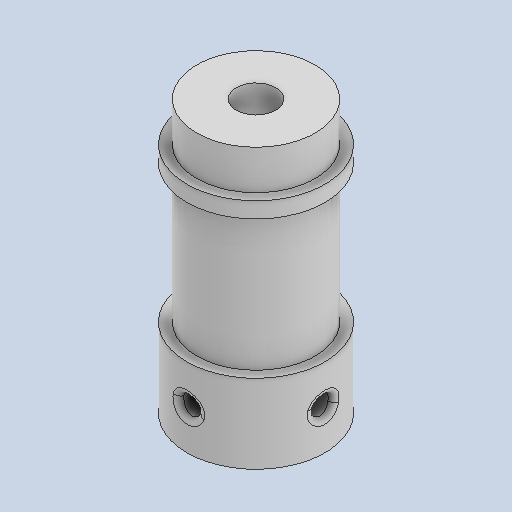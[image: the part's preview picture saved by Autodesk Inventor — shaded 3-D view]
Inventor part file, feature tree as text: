
AUTODESK INVENTOR PART (.ipt)
format: ipt  version: 2023 (Build 270158000, 158)  size: 195,584 bytes
history: native  units: mm
features: fillet x1
ambient origin geometry x8: Origin, YZ Plane, XZ Plane, XY Plane, X Axis, Y Axis, Z Axis, Center Point
bodies: Solid1 (feature_tree)
feature tree (1):
  fillet  "Fillet1"  [1 undecoded]
note: 1 required parameter value undecoded (feature->parameter linkage not recoverable at this tier; creation-order binding heuristic only, values carry confidence <= 0.55)
